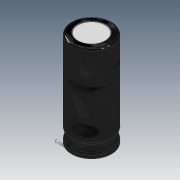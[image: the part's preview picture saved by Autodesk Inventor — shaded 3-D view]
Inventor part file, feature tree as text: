
AUTODESK INVENTOR PART (.ipt)
format: ipt  version: 2020 (Build 240168000, 168)  size: 231,424 bytes
history: native  units: in
note: dims shown in document units (in); Inventor stores cm internally (conversion verified against a paired STEP export)
features: fillet x4, sketch x3, revolve x1, plane x1, sweep x1, mirror x1
ambient origin geometry x8: Origin, YZ Plane, XZ Plane, XY Plane, X Axis, Y Axis, Z Axis, Center Point
bodies: Solid1 (feature_tree)
feature tree (11):
  revolve  "Revolution1"  [1 undecoded]
  fillet  "Fillet1"  Radius=0.0039in
  fillet  "Fillet2"  Radius=0.0512in
  fillet  "Fillet3"  Radius=0.1378in
  fillet  "Fillet4"  Radius=0.0157in
  sketch  "Sketch2"  dims[d8=90.0deg d9=0.0039in]
  plane  "Work Plane1"
  sweep  "Sweep1"
  mirror  "Mirror1"
  sketch  "Sketch1"  dims[d0=0.4016in d1=0.9567in d2=0.1378in d3=0.0039in d4=0.0512in d5=0.1378in d6=0.0157in d7=0.0433in]
  sketch  "Sketch3"  dims[d10=0.0197in d11=0.0394in d12=0.0118in d13=0.2283in d14=0.0276in d15=90.0deg d16=0.0394in d17=0.1969in d18=0.0in d19=0.0in]
note: 1 required parameter value undecoded (feature->parameter linkage not recoverable at this tier; creation-order binding heuristic only, values carry confidence <= 0.55)
